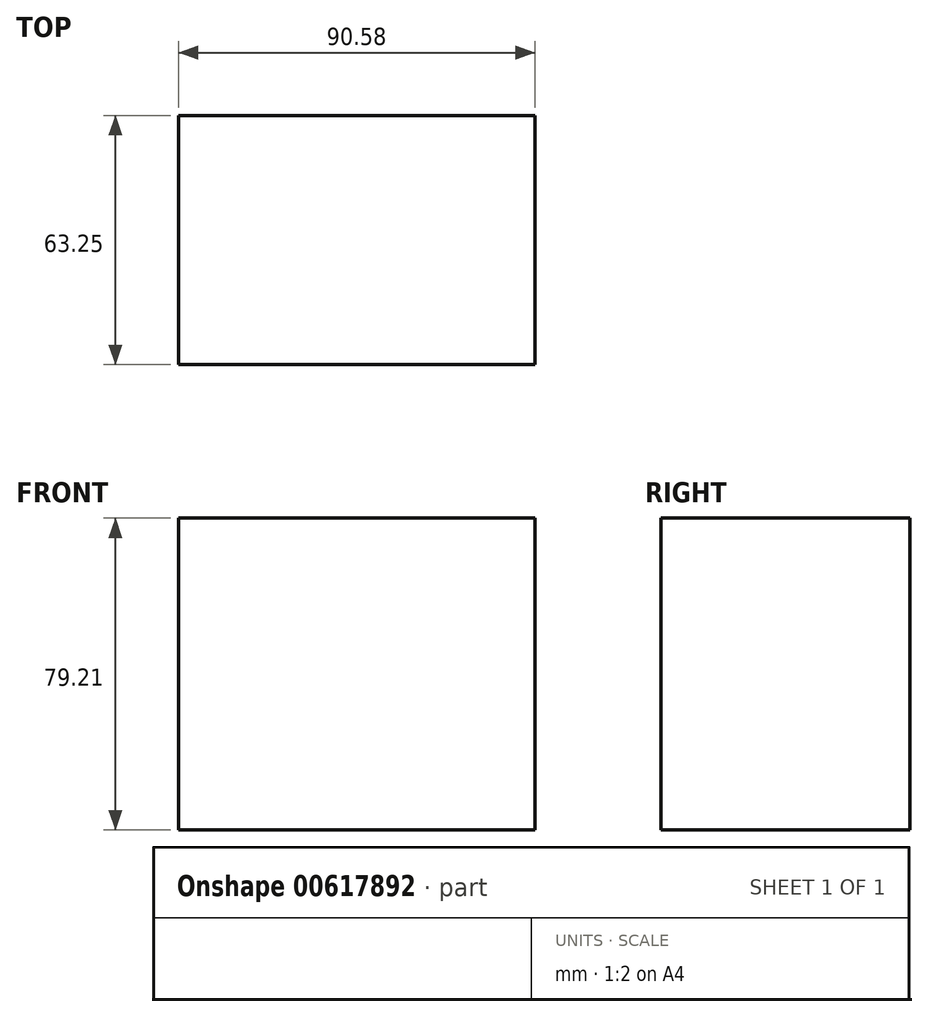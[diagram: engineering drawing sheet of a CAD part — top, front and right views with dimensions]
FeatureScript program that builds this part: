
annotation { "Feature Type Name" : "Feature", "Feature Type Description" : "" }
export const myFeature = defineFeature(function(context is Context, id is Id, definition is map)
    precondition{}
    {
        {
            var Q0;
            Q0=qCreatedBy(makeId("Front.planeOp"),FACE);
            var sketch = newSketch(context, id + "F0", { "sketchPlane" : qUnion([Q0])});
            skLineSegment(sketch, "E0.bottom", {"start": v(-5.48, 34.5) * mm, "end": v(-96.06, 34.5) * mm});
            skLineSegment(sketch, "E0.top", {"start": v(-5.48, -44.71) * mm, "end": v(-96.06, -44.71) * mm});
            skLineSegment(sketch, "E0.left", {"start": v(-5.48, 34.5) * mm, "end": v(-5.48, -44.71) * mm});
            skLineSegment(sketch, "E0.right", {"start": v(-96.06, 34.5) * mm, "end": v(-96.06, -44.71) * mm});
            skSolve(sketch);
        }
        {
            var Q0;
            Q0 = qSketchRegion(id + "F0", true);
            extrude(context, id + "F1", {"entities" : qUnion([Q0]), "oppositeDirection" : true, "depth" : 63.25 * mm, "offsetDistance" : 25.4 * mm});
        }
    });
